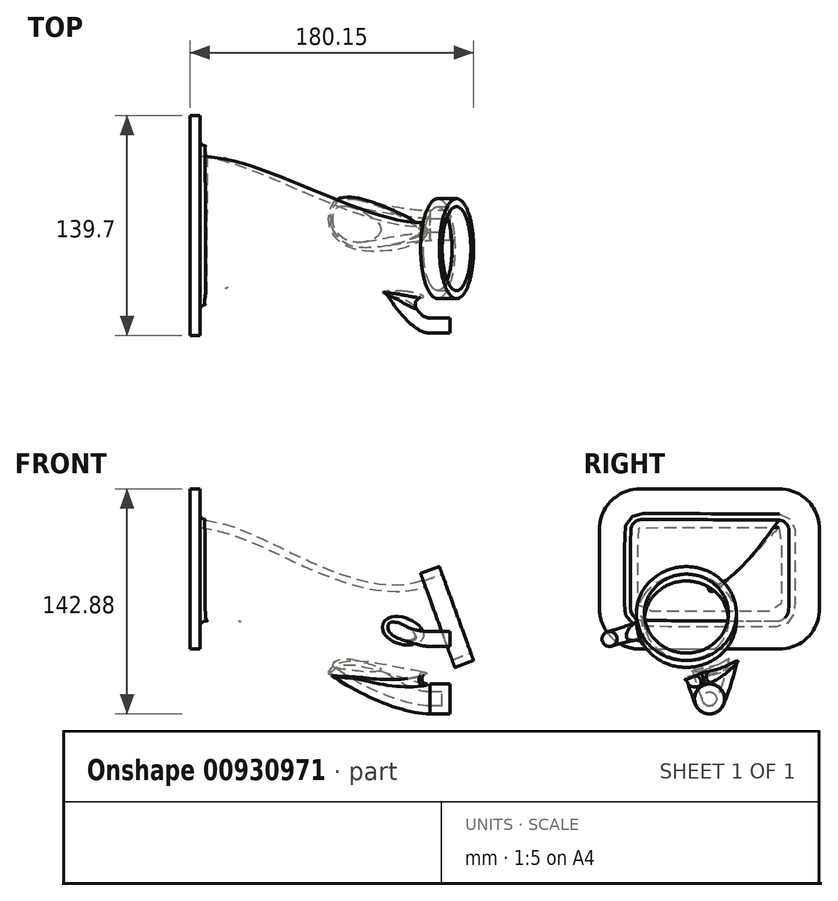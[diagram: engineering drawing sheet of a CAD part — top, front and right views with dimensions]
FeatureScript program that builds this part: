
annotation { "Feature Type Name" : "Feature", "Feature Type Description" : "" }
export const myFeature = defineFeature(function(context is Context, id is Id, definition is map)
    precondition{}
    {
        {
            var Q0;
            Q0=qCreatedBy(makeId("Right.planeOp"),FACE);
            cPlane(context, id + "F0", {"entities" : qUnion([Q0]), "cplaneType" : CPlaneType.OFFSET, "offset" : 76.2 * mm, "width" : 152.4 * mm, "height" : 152.4 * mm});
        }
        {
            var Q0;
            Q0=qCreatedBy(makeId("Right.planeOp"),FACE);
            cPlane(context, id + "F1", {"entities" : qUnion([Q0]), "cplaneType" : CPlaneType.OFFSET, "offset" : 76.2 * mm, "oppositeDirection" : true, "width" : 152.4 * mm, "height" : 152.4 * mm});
        }
        {
            var Q0;
            Q0=qCreatedBy(id+"F1.planeOp",FACE);
            var sketch = newSketch(context, id + "F2", { "sketchPlane" : qUnion([Q0])});
            skLineSegment(sketch, "E0.bottom", {"start": v(44.45, 57.15) * mm, "end": v(-44.45, 57.15) * mm});
            skLineSegment(sketch, "E0.top", {"start": v(44.45, -6.35) * mm, "end": v(-44.45, -6.35) * mm});
            skLineSegment(sketch, "E0.left", {"start": v(50.8, 50.8) * mm, "end": v(50.8, 0) * mm});
            skLineSegment(sketch, "E0.right", {"start": v(-50.8, 50.8) * mm, "end": v(-50.8, 0) * mm});
            skPoint(sketch, "E0.middle", {"position": v(0, 25.4) * mm});
            skPoint(sketch, "E1.visualSharp", {"position": v(-50.8, 57.15) * mm});
            skArc(sketch, "E1.filletArc", {"start": v(-44.45, 57.15) * mm, "mid": v(-48.94, 55.3) * mm, "end": v(-50.8, 50.8) * mm});
            skPoint(sketch, "E2.visualSharp", {"position": v(50.8, 57.15) * mm});
            skArc(sketch, "E2.filletArc", {"start": v(50.8, 50.8) * mm, "mid": v(48.94, 55.3) * mm, "end": v(44.45, 57.15) * mm});
            skPoint(sketch, "E3.visualSharp", {"position": v(50.8, -6.35) * mm});
            skArc(sketch, "E3.filletArc", {"start": v(44.45, -6.35) * mm, "mid": v(48.94, -4.5) * mm, "end": v(50.8, 0) * mm});
            skPoint(sketch, "E4.visualSharp", {"position": v(-50.8, -6.35) * mm});
            skArc(sketch, "E4.filletArc", {"start": v(-50.8, 0) * mm, "mid": v(-48.94, -4.5) * mm, "end": v(-44.45, -6.35) * mm});
            skSolve(sketch);
        }
        {
            var Q0;
            Q0=qCreatedBy(makeId("Right.planeOp"),FACE);
            var sketch = newSketch(context, id + "F3", { "sketchPlane" : qUnion([Q0])});
            skCircle(sketch, "E5", {"center": v(0, 0) * mm, "radius": 38.1 * mm});
            skSolve(sketch);
        }
        {
            var Q0;
            Q0=qCreatedBy(id+"F0.planeOp",FACE);
            var sketch = newSketch(context, id + "F4", { "sketchPlane" : qUnion([Q0])});
            skLineSegment(sketch, "E6", {"start": v(65.38, 6.35) * mm, "end": v(-65.38, 6.35) * mm, "construction": true});
            skSolve(sketch);
        }
        {
            var Q0;
            Q0=sQuery(id+"F4.wireOp",EDGE,"E6");
            cPlane(context, id + "F5", {"entities" : qUnion([Q0]), "cplaneType" : CPlaneType.LINE_ANGLE, "offset" : 25.4 * mm, "angle" : 70 * degree, "oppositeDirection" : true, "width" : 152.4 * mm, "height" : 152.4 * mm});
        }
        {
            var Q0;
            Q0=qCreatedBy(id+"F5.planeOp",FACE);
            var sketch = newSketch(context, id + "F6", { "sketchPlane" : qUnion([Q0])});
            skCircle(sketch, "E7", {"center": v(14.69, -34.6) * mm, "radius": 31.75 * mm});
            skSolve(sketch);
        }
        {
            var Q0;
            Q0=makeQuery(id+"F2.imprint","IMPRINT",FACE,{"disambiguationData":[TD([[makeQuery(id+"F2.imprint","IMPRINT",EDGE,{"derivedFrom":sQuery(id+"F2.wireOp",EDGE,"E0.bottom")}),1.0]])]});
            var Q1;
            Q1=makeQuery(id+"F3.imprint","IMPRINT",FACE,{"disambiguationData":[TD([[makeQuery(id+"F3.imprint","IMPRINT",EDGE,{"derivedFrom":sQuery(id+"F3.wireOp",EDGE,"E5")}),1.0]])]});
            var Q2;
            Q2=makeQuery(id+"F6.imprint","IMPRINT",FACE,{"disambiguationData":[TD([[makeQuery(id+"F6.imprint","IMPRINT",EDGE,{"derivedFrom":sQuery(id+"F6.wireOp",EDGE,"E7")}),1.0]])]});
            loft(context, id + "F7", {"startCondition" : LoftEndDerivativeType.NORMAL_TO_PROFILE, "startMagnitude" : 1, "endCondition" : LoftEndDerivativeType.NORMAL_TO_PROFILE, "endMagnitude" : 1, "sheetProfilesArray" : [{ "sheetProfileEntities" : qUnion([Q0]) }, { "sheetProfileEntities" : qUnion([Q1]) }, { "sheetProfileEntities" : qUnion([Q2]) }]});
        }
        {
            var Q0;
            Q0=makeQuery(id+"F7.opLoft","CAP_FACE",FACE,{"disambiguationData":[OSD([makeQuery(id+"F6.imprint","IMPRINT",FACE,{"disambiguationData":[TD([[makeQuery(id+"F6.imprint","IMPRINT",EDGE,{"derivedFrom":sQuery(id+"F6.wireOp",EDGE,"E7")}),1.0]])]})])],"isStart":true});
            extrude(context, id + "F8", {"entities" : qUnion([Q0]), "operationType" : NewBodyOperationType.ADD, "depth" : 12.7 * mm, "offsetDistance" : 25.4 * mm});
        }
        {
            var Q0;
            Q0=qCreatedBy(id+"F1.planeOp",FACE);
            cPlane(context, id + "F9", {"entities" : qUnion([Q0]), "cplaneType" : CPlaneType.OFFSET, "offset" : 152.4 * mm, "width" : 152.4 * mm, "height" : 152.4 * mm});
        }
        {
            var Q0;
            Q0=qCreatedBy(id+"F9.planeOp",FACE);
            var sketch = newSketch(context, id + "F10", { "sketchPlane" : qUnion([Q0])});
            skCircle(sketch, "E8", {"center": v(0, -57.15) * mm, "radius": 9.53 * mm});
            skSolve(sketch);
        }
        {
            var Q0;
            Q0=qCreatedBy(makeId("Right.planeOp"),FACE);
            var sketch = newSketch(context, id + "F11", { "sketchPlane" : qUnion([Q0])});
            skCircle(sketch, "E9", {"center": v(0, -12.7) * mm, "radius": 12.7 * mm});
            skSolve(sketch);
        }
        {
            var Q1;
            Q1=makeQuery(id+"F10.imprint","IMPRINT",FACE,{"disambiguationData":[TD([[makeQuery(id+"F10.imprint","IMPRINT",EDGE,{"derivedFrom":sQuery(id+"F10.wireOp",EDGE,"E8")}),1.0]])]});
            var Q2;
            Q2 = qSketchRegion(id + "F11", true);
            loft(context, id + "F12", {"operationType" : NewBodyOperationType.ADD, "startCondition" : LoftEndDerivativeType.NORMAL_TO_PROFILE, "startMagnitude" : 1, "endCondition" : LoftEndDerivativeType.TANGENT_TO_PROFILE, "endMagnitude" : 1, "sheetProfilesArray" : [{ "sheetProfileEntities" : qUnion([Q1]) }, { "sheetProfileEntities" : qUnion([Q2]) }]});
        }
        {
            var Q0;
            Q0=qCreatedBy(id+"F9.planeOp",FACE);
            var sketch = newSketch(context, id + "F13", { "sketchPlane" : qUnion([Q0])});
            skCircle(sketch, "E10", {"center": v(-63.5, -19.05) * mm, "radius": 4.76 * mm});
            skSolve(sketch);
        }
        {
            var Q0;
            Q0=qCreatedBy(makeId("Front.planeOp"),FACE);
            var sketch = newSketch(context, id + "F14", { "sketchPlane" : qUnion([Q0])});
            skCircle(sketch, "E11", {"center": v(38.1, 0) * mm, "radius": 12.7 * mm});
            skSolve(sketch);
        }
        {
            var Q1;
            Q1=makeQuery(id+"F13.imprint","IMPRINT",FACE,{"disambiguationData":[TD([[makeQuery(id+"F13.imprint","IMPRINT",EDGE,{"derivedFrom":sQuery(id+"F13.wireOp",EDGE,"E10")}),1.0]])]});
            var Q2;
            Q2 = qSketchRegion(id + "F14", true);
            loft(context, id + "F15", {"operationType" : NewBodyOperationType.ADD, "startCondition" : LoftEndDerivativeType.NORMAL_TO_PROFILE, "startMagnitude" : 1, "sheetProfilesArray" : [{ "sheetProfileEntities" : qUnion([Q1]) }, { "sheetProfileEntities" : qUnion([Q2]) }]});
        }
        {
            var Q0;
            Q0=makeQuery(id+"F15.opLoft","CAP_FACE",FACE,{"disambiguationData":[OSD([makeQuery(id+"F13.imprint","IMPRINT",FACE,{"disambiguationData":[TD([[makeQuery(id+"F13.imprint","IMPRINT",EDGE,{"derivedFrom":sQuery(id+"F13.wireOp",EDGE,"E10")}),1.0]])]})])],"isStart":true});
            extrude(context, id + "F16", {"entities" : qUnion([Q0]), "operationType" : NewBodyOperationType.ADD, "depth" : 12.7 * mm, "offsetDistance" : 25.4 * mm});
        }
        {
            var Q0;
            Q0=makeQuery(id+"F12.opLoft","CAP_FACE",FACE,{"disambiguationData":[OSD([makeQuery(id+"F10.imprint","IMPRINT",FACE,{"disambiguationData":[TD([[makeQuery(id+"F10.imprint","IMPRINT",EDGE,{"derivedFrom":sQuery(id+"F10.wireOp",EDGE,"E8")}),1.0]])]})])],"isStart":true});
            extrude(context, id + "F17", {"entities" : qUnion([Q0]), "operationType" : NewBodyOperationType.ADD, "depth" : 12.7 * mm, "offsetDistance" : 25.4 * mm});
        }
        {
            var Q0;
            Q0=makeQuery(id+"F8.opExtrude","CAP_FACE",FACE,{"disambiguationData":[OSD([makeQuery(id+"F6.imprint","IMPRINT",FACE,{"disambiguationData":[TD([[makeQuery(id+"F6.imprint","IMPRINT",EDGE,{"derivedFrom":sQuery(id+"F6.wireOp",EDGE,"E7")}),1.0]])]})])],"isStart":false});
            var Q1;
            Q1=makeQuery(id+"F7.opLoft","CAP_FACE",FACE,{"disambiguationData":[OSD([makeQuery(id+"F2.imprint","IMPRINT",FACE,{"disambiguationData":[TD([[makeQuery(id+"F2.imprint","IMPRINT",EDGE,{"derivedFrom":sQuery(id+"F2.wireOp",EDGE,"E0.bottom")}),1.0]])]})])],"isStart":true});
            shell(context, id + "F18", {"entities" : qUnion([Q0, Q1]), "thickness" : 5.08 * mm});
        }
        {
            var Q0;
            Q0=qCreatedBy(id+"F1.planeOp",FACE);
            var sketch = newSketch(context, id + "F19", { "sketchPlane" : qUnion([Q0])});
            skFitSpline(sketch, "E12.0", {"points": [v(69.85, 50.8) * mm, v(69.85, 51.31) * mm, v(69.82, 52.32) * mm, v(69.69, 53.78) * mm, v(69.52, 54.93) * mm, v(69.35, 55.8) * mm, v(69.22, 56.44) * mm, v(69.07, 57.06) * mm, v(68.85, 57.87) * mm, v(68.55, 58.86) * mm, v(68.21, 59.8) * mm, v(67.92, 60.5) * mm, v(67.7, 61.02) * mm, v(67.48, 61.53) * mm, v(67.16, 62.19) * mm, v(66.74, 63) * mm, v(66.3, 63.77) * mm, v(65.93, 64.37) * mm, v(65.65, 64.8) * mm, v(65.36, 65.22) * mm, v(64.97, 65.78) * mm, v(64.45, 66.47) * mm, v(63.9, 67.14) * mm, v(63.46, 67.65) * mm, v(63.12, 68.03) * mm, v(62.77, 68.4) * mm, v(62.29, 68.89) * mm, v(61.65, 69.5) * mm, v(60.98, 70.09) * mm, v(60.43, 70.55) * mm, v(60, 70.88) * mm, v(59.57, 71.21) * mm, v(58.96, 71.65) * mm, v(58.16, 72.2) * mm, v(57.3, 72.71) * mm, v(56.6, 73.1) * mm, v(56.06, 73.4) * mm, v(55.5, 73.67) * mm, v(54.72, 74.04) * mm, v(53.68, 74.48) * mm, v(52.58, 74.87) * mm, v(51.66, 75.16) * mm, v(50.96, 75.36) * mm, v(50.24, 75.54) * mm, v(49.23, 75.76) * mm, v(47.9, 75.98) * mm, v(46.22, 76.16) * mm, v(45.04, 76.2) * mm, v(44.45, 76.2) * mm]});
            skFitSpline(sketch, "E12.1", {"points": [v(69.85, 0) * mm, v(69.85, 16.93) * mm, v(69.85, 33.87) * mm, v(69.85, 50.8) * mm]});
            skFitSpline(sketch, "E12.2", {"points": [v(44.45, 76.2) * mm, v(14.82, 76.2) * mm, v(-14.82, 76.2) * mm, v(-44.45, 76.2) * mm]});
            skFitSpline(sketch, "E12.3", {"points": [v(44.45, -25.4) * mm, v(45.04, -25.4) * mm, v(46.22, -25.36) * mm, v(47.9, -25.18) * mm, v(49.23, -24.96) * mm, v(50.24, -24.74) * mm, v(50.96, -24.56) * mm, v(51.66, -24.36) * mm, v(52.58, -24.07) * mm, v(53.68, -23.68) * mm, v(54.72, -23.24) * mm, v(55.5, -22.87) * mm, v(56.06, -22.6) * mm, v(56.6, -22.3) * mm, v(57.3, -21.91) * mm, v(58.16, -21.4) * mm, v(58.96, -20.85) * mm, v(59.57, -20.41) * mm, v(60, -20.08) * mm, v(60.43, -19.75) * mm, v(60.98, -19.29) * mm, v(61.65, -18.7) * mm, v(62.29, -18.09) * mm, v(62.77, -17.6) * mm, v(63.12, -17.23) * mm, v(63.46, -16.85) * mm, v(63.9, -16.34) * mm, v(64.45, -15.67) * mm, v(64.97, -14.98) * mm, v(65.36, -14.42) * mm, v(65.65, -14) * mm, v(65.93, -13.57) * mm, v(66.3, -12.97) * mm, v(66.74, -12.2) * mm, v(67.16, -11.39) * mm, v(67.48, -10.73) * mm, v(67.7, -10.22) * mm, v(67.92, -9.7) * mm, v(68.21, -9) * mm, v(68.55, -8.06) * mm, v(68.85, -7.07) * mm, v(69.07, -6.26) * mm, v(69.22, -5.64) * mm, v(69.35, -5) * mm, v(69.52, -4.13) * mm, v(69.69, -2.98) * mm, v(69.82, -1.52) * mm, v(69.85, -0.51) * mm, v(69.85, 0) * mm]});
            skFitSpline(sketch, "E12.4", {"points": [v(-44.45, 76.2) * mm, v(-45.04, 76.2) * mm, v(-46.22, 76.16) * mm, v(-47.9, 75.98) * mm, v(-49.23, 75.76) * mm, v(-50.24, 75.54) * mm, v(-50.96, 75.36) * mm, v(-51.66, 75.16) * mm, v(-52.58, 74.87) * mm, v(-53.68, 74.48) * mm, v(-54.72, 74.04) * mm, v(-55.5, 73.67) * mm, v(-56.06, 73.4) * mm, v(-56.6, 73.1) * mm, v(-57.3, 72.71) * mm, v(-58.16, 72.2) * mm, v(-58.96, 71.65) * mm, v(-59.57, 71.21) * mm, v(-60, 70.88) * mm, v(-60.43, 70.55) * mm, v(-60.98, 70.09) * mm, v(-61.65, 69.5) * mm, v(-62.29, 68.89) * mm, v(-62.77, 68.4) * mm, v(-63.12, 68.03) * mm, v(-63.46, 67.65) * mm, v(-63.9, 67.14) * mm, v(-64.45, 66.47) * mm, v(-64.97, 65.78) * mm, v(-65.36, 65.22) * mm, v(-65.65, 64.8) * mm, v(-65.93, 64.37) * mm, v(-66.3, 63.77) * mm, v(-66.74, 63) * mm, v(-67.16, 62.19) * mm, v(-67.48, 61.53) * mm, v(-67.7, 61.02) * mm, v(-67.92, 60.5) * mm, v(-68.21, 59.8) * mm, v(-68.55, 58.86) * mm, v(-68.85, 57.87) * mm, v(-69.07, 57.06) * mm, v(-69.22, 56.44) * mm, v(-69.35, 55.8) * mm, v(-69.52, 54.93) * mm, v(-69.69, 53.78) * mm, v(-69.82, 52.32) * mm, v(-69.85, 51.31) * mm, v(-69.85, 50.8) * mm]});
            skFitSpline(sketch, "E12.5", {"points": [v(-69.85, 50.8) * mm, v(-69.85, 33.87) * mm, v(-69.85, 16.93) * mm, v(-69.85, 0) * mm]});
            skFitSpline(sketch, "E12.6", {"points": [v(-69.85, 0) * mm, v(-69.85, -0.51) * mm, v(-69.82, -1.52) * mm, v(-69.69, -2.98) * mm, v(-69.52, -4.13) * mm, v(-69.35, -5) * mm, v(-69.22, -5.64) * mm, v(-69.07, -6.26) * mm, v(-68.85, -7.07) * mm, v(-68.55, -8.06) * mm, v(-68.21, -9) * mm, v(-67.92, -9.7) * mm, v(-67.7, -10.22) * mm, v(-67.48, -10.73) * mm, v(-67.16, -11.39) * mm, v(-66.74, -12.2) * mm, v(-66.3, -12.97) * mm, v(-65.93, -13.57) * mm, v(-65.65, -14) * mm, v(-65.36, -14.42) * mm, v(-64.97, -14.98) * mm, v(-64.45, -15.67) * mm, v(-63.9, -16.34) * mm, v(-63.46, -16.85) * mm, v(-63.12, -17.23) * mm, v(-62.77, -17.6) * mm, v(-62.29, -18.09) * mm, v(-61.65, -18.7) * mm, v(-60.98, -19.29) * mm, v(-60.43, -19.75) * mm, v(-60, -20.08) * mm, v(-59.57, -20.41) * mm, v(-58.96, -20.85) * mm, v(-58.16, -21.4) * mm, v(-57.3, -21.91) * mm, v(-56.6, -22.3) * mm, v(-56.06, -22.6) * mm, v(-55.5, -22.87) * mm, v(-54.72, -23.24) * mm, v(-53.68, -23.68) * mm, v(-52.58, -24.07) * mm, v(-51.66, -24.36) * mm, v(-50.96, -24.56) * mm, v(-50.24, -24.74) * mm, v(-49.23, -24.96) * mm, v(-47.9, -25.18) * mm, v(-46.22, -25.36) * mm, v(-45.04, -25.4) * mm, v(-44.45, -25.4) * mm]});
            skFitSpline(sketch, "E12.7", {"points": [v(-44.45, -25.4) * mm, v(-14.82, -25.4) * mm, v(14.82, -25.4) * mm, v(44.45, -25.4) * mm]});
            skFitSpline(sketch, "E13.0", {"points": [v(-45.46, -3.67) * mm, v(-45.36, -3.7) * mm, v(-45.26, -3.72) * mm, v(-45.16, -3.74) * mm, v(-45.06, -3.76) * mm, v(-44.95, -3.78) * mm, v(-44.85, -3.8) * mm, v(-44.74, -3.8) * mm, v(-44.65, -3.8) * mm, v(-44.52, -3.81) * mm, v(-44.43, -3.81) * mm, v(-44.36, -3.81) * mm, v(-44.33, -3.8) * mm, v(-44.31, -3.8) * mm, v(-44.28, -3.8) * mm, v(-44.22, -3.81) * mm, v(-44.15, -3.81) * mm, v(-44.06, -3.81) * mm, v(-43.94, -3.8) * mm, v(-43.81, -3.8) * mm, v(-43.63, -3.81) * mm, v(-43.4, -3.81) * mm, v(-43.14, -3.8) * mm, v(-42.87, -3.8) * mm, v(-42.51, -3.81) * mm, v(-42.06, -3.8) * mm, v(-41.52, -3.81) * mm, v(-40.99, -3.81) * mm, v(-40.27, -3.8) * mm, v(-39.37, -3.81) * mm, v(-38.3, -3.8) * mm, v(-37.22, -3.81) * mm, v(-36.14, -3.8) * mm, v(-35.07, -3.8) * mm, v(-33.63, -3.81) * mm, v(-31.84, -3.8) * mm, v(-29.69, -3.81) * mm, v(-27.54, -3.8) * mm, v(-25.38, -3.81) * mm, v(-22.51, -3.8) * mm, v(-18.93, -3.81) * mm, v(-14.62, -3.8) * mm, v(-10.32, -3.81) * mm, v(-6.01, -3.8) * mm, v(-1.7, -3.81) * mm, v(2.6, -3.8) * mm, v(6.9, -3.81) * mm, v(11.2, -3.8) * mm, v(15.5, -3.81) * mm, v(19.1, -3.8) * mm, v(21.97, -3.81) * mm, v(24.12, -3.81) * mm, v(26.27, -3.8) * mm, v(28.42, -3.81) * mm, v(30.57, -3.8) * mm, v(32.37, -3.81) * mm, v(33.8, -3.8) * mm, v(34.88, -3.8) * mm, v(35.96, -3.81) * mm, v(37.03, -3.81) * mm, v(38.1, -3.8) * mm, v(39.18, -3.81) * mm, v(40.08, -3.8) * mm, v(40.8, -3.81) * mm, v(41.34, -3.81) * mm, v(41.87, -3.8) * mm, v(42.41, -3.81) * mm, v(42.86, -3.8) * mm, v(43.17, -3.81) * mm, v(43.35, -3.81) * mm, v(43.49, -3.81) * mm, v(43.62, -3.8) * mm, v(43.76, -3.8) * mm, v(43.89, -3.81) * mm, v(44.03, -3.81) * mm, v(44.15, -3.8) * mm, v(44.21, -3.8) * mm, v(44.25, -3.8) * mm, v(44.27, -3.8) * mm, v(44.3, -3.81) * mm, v(44.35, -3.81) * mm, v(44.44, -3.81) * mm, v(44.57, -3.8) * mm, v(44.69, -3.8) * mm, v(44.79, -3.8) * mm, v(44.9, -3.79) * mm, v(45.03, -3.77) * mm, v(45.2, -3.74) * mm, v(45.4, -3.7) * mm, v(45.65, -3.62) * mm, v(45.97, -3.5) * mm, v(46.33, -3.32) * mm, v(46.67, -3.1) * mm, v(46.99, -2.85) * mm, v(47.27, -2.57) * mm, v(47.53, -2.26) * mm, v(47.75, -1.92) * mm, v(47.94, -1.55) * mm, v(48.06, -1.24) * mm, v(48.13, -0.99) * mm, v(48.18, -0.8) * mm, v(48.2, -0.64) * mm, v(48.23, -0.5) * mm, v(48.24, -0.38) * mm, v(48.25, -0.27) * mm, v(48.26, -0.14) * mm, v(48.26, -0.02) * mm, v(48.26, 0.07) * mm, v(48.26, 0.12) * mm, v(48.26, 0.15) * mm, v(48.26, 0.18) * mm, v(48.26, 0.22) * mm, v(48.26, 0.27) * mm, v(48.26, 0.34) * mm, v(48.26, 0.43) * mm, v(48.26, 0.55) * mm, v(48.26, 0.68) * mm, v(48.26, 0.86) * mm, v(48.26, 1.09) * mm, v(48.26, 1.36) * mm, v(48.26, 1.63) * mm, v(48.26, 1.99) * mm, v(48.26, 2.44) * mm, v(48.26, 2.98) * mm, v(48.26, 3.52) * mm, v(48.26, 4.06) * mm, v(48.26, 4.79) * mm, v(48.26, 5.69) * mm, v(48.26, 6.77) * mm, v(48.26, 7.85) * mm, v(48.26, 8.94) * mm, v(48.26, 10.38) * mm, v(48.26, 12.19) * mm, v(48.26, 14.35) * mm, v(48.26, 16.52) * mm, v(48.26, 18.68) * mm, v(48.26, 20.85) * mm, v(48.26, 23.02) * mm, v(48.26, 25.9) * mm, v(48.26, 28.8) * mm, v(48.26, 31.68) * mm, v(48.26, 33.84) * mm, v(48.26, 36) * mm, v(48.26, 38.18) * mm, v(48.26, 39.98) * mm, v(48.26, 41.42) * mm, v(48.26, 42.5) * mm, v(48.26, 43.59) * mm, v(48.26, 44.67) * mm, v(48.26, 45.76) * mm, v(48.26, 46.66) * mm, v(48.26, 47.38) * mm, v(48.26, 47.92) * mm, v(48.26, 48.37) * mm, v(48.26, 48.73) * mm, v(48.26, 49) * mm, v(48.26, 49.27) * mm, v(48.26, 49.55) * mm, v(48.26, 49.82) * mm, v(48.26, 50.04) * mm, v(48.26, 50.22) * mm, v(48.26, 50.36) * mm, v(48.26, 50.47) * mm, v(48.26, 50.56) * mm, v(48.26, 50.62) * mm, v(48.26, 50.68) * mm, v(48.26, 50.73) * mm, v(48.26, 50.77) * mm, v(48.26, 50.82) * mm, v(48.26, 50.89) * mm, v(48.26, 50.97) * mm, v(48.25, 51.07) * mm, v(48.24, 51.18) * mm, v(48.23, 51.33) * mm, v(48.2, 51.5) * mm, v(48.15, 51.71) * mm, v(48.08, 51.98) * mm, v(47.98, 52.24) * mm, v(47.86, 52.5) * mm, v(47.76, 52.7) * mm, v(47.64, 52.88) * mm, v(47.48, 53.12) * mm, v(47.25, 53.4) * mm, v(46.94, 53.7) * mm, v(46.6, 53.96) * mm, v(46.23, 54.18) * mm, v(45.9, 54.33) * mm, v(45.62, 54.43) * mm, v(45.42, 54.49) * mm, v(45.22, 54.53) * mm, v(45.04, 54.57) * mm, v(44.88, 54.59) * mm, v(44.78, 54.6) * mm, v(44.67, 54.6) * mm, v(44.54, 54.6) * mm, v(44.43, 54.61) * mm, v(44.36, 54.61) * mm, v(44.33, 54.6) * mm, v(44.3, 54.6) * mm, v(44.26, 54.6) * mm, v(44.2, 54.6) * mm, v(44.14, 54.6) * mm, v(44.04, 54.61) * mm, v(43.92, 54.61) * mm, v(43.77, 54.6) * mm, v(43.63, 54.6) * mm, v(43.44, 54.6) * mm, v(43.2, 54.61) * mm, v(42.92, 54.61) * mm, v(42.63, 54.6) * mm, v(42.35, 54.6) * mm, v(41.97, 54.61) * mm, v(41.5, 54.6) * mm, v(40.92, 54.6) * mm, v(40.35, 54.61) * mm, v(39.78, 54.61) * mm, v(39.02, 54.6) * mm, v(38.07, 54.61) * mm, v(36.92, 54.6) * mm, v(35.78, 54.6) * mm, v(34.64, 54.61) * mm, v(33.5, 54.61) * mm, v(31.97, 54.6) * mm, v(30.07, 54.61) * mm, v(27.79, 54.6) * mm, v(25.5, 54.61) * mm, v(23.22, 54.6) * mm, v(20.93, 54.6) * mm, v(17.89, 54.61) * mm, v(14.08, 54.6) * mm, v(9.51, 54.61) * mm, v(4.94, 54.6) * mm, v(0.37, 54.6) * mm, v(-4.2, 54.61) * mm, v(-8.76, 54.6) * mm, v(-13.33, 54.61) * mm, v(-17.14, 54.6) * mm, v(-20.18, 54.61) * mm, v(-22.47, 54.61) * mm, v(-24.75, 54.6) * mm, v(-27.04, 54.61) * mm, v(-29.32, 54.6) * mm, v(-31.6, 54.61) * mm, v(-33.5, 54.6) * mm, v(-35.03, 54.61) * mm, v(-36.17, 54.61) * mm, v(-37.32, 54.6) * mm, v(-38.46, 54.61) * mm, v(-39.4, 54.6) * mm, v(-40.17, 54.61) * mm, v(-40.74, 54.61) * mm, v(-41.31, 54.6) * mm, v(-41.88, 54.6) * mm, v(-42.36, 54.61) * mm, v(-42.74, 54.6) * mm, v(-43.03, 54.6) * mm, v(-43.31, 54.61) * mm, v(-43.55, 54.61) * mm, v(-43.74, 54.6) * mm, v(-43.88, 54.6) * mm, v(-44, 54.61) * mm, v(-44.1, 54.61) * mm, v(-44.17, 54.61) * mm, v(-44.23, 54.6) * mm, v(-44.27, 54.6) * mm, v(-44.3, 54.6) * mm, v(-44.33, 54.61) * mm, v(-44.39, 54.61) * mm, v(-44.49, 54.61) * mm, v(-44.63, 54.6) * mm, v(-44.76, 54.6) * mm, v(-44.88, 54.59) * mm, v(-45, 54.57) * mm, v(-45.15, 54.55) * mm, v(-45.33, 54.5) * mm, v(-45.54, 54.45) * mm, v(-45.81, 54.36) * mm, v(-46.1, 54.24) * mm, v(-46.36, 54.1) * mm, v(-46.62, 53.94) * mm, v(-46.93, 53.7) * mm, v(-47.25, 53.4) * mm, v(-47.54, 53.04) * mm, v(-47.79, 52.65) * mm, v(-47.98, 52.25) * mm, v(-48.1, 51.9) * mm, v(-48.18, 51.6) * mm, v(-48.22, 51.37) * mm, v(-48.24, 51.18) * mm, v(-48.25, 51.04) * mm, v(-48.26, 50.93) * mm, v(-48.26, 50.83) * mm, v(-48.26, 50.76) * mm, v(-48.26, 50.7) * mm, v(-48.26, 50.67) * mm, v(-48.26, 50.64) * mm, v(-48.26, 50.6) * mm, v(-48.26, 50.54) * mm, v(-48.26, 50.47) * mm, v(-48.26, 50.36) * mm, v(-48.26, 50.23) * mm, v(-48.26, 50.08) * mm, v(-48.26, 49.93) * mm, v(-48.26, 49.78) * mm, v(-48.26, 49.62) * mm, v(-48.26, 49.42) * mm, v(-48.26, 49.17) * mm, v(-48.26, 48.86) * mm, v(-48.26, 48.56) * mm, v(-48.26, 48.15) * mm, v(-48.26, 47.64) * mm, v(-48.26, 47.03) * mm, v(-48.26, 46.43) * mm, v(-48.26, 45.82) * mm, v(-48.26, 45.2) * mm, v(-48.26, 44.4) * mm, v(-48.26, 43.38) * mm, v(-48.26, 42.16) * mm, v(-48.26, 40.94) * mm, v(-48.26, 39.73) * mm, v(-48.26, 38.5) * mm, v(-48.26, 36.89) * mm, v(-48.26, 34.86) * mm, v(-48.26, 32.42) * mm, v(-48.26, 29.98) * mm, v(-48.26, 27.55) * mm, v(-48.26, 25.11) * mm, v(-48.26, 22.68) * mm, v(-48.26, 20.24) * mm, v(-48.26, 17.8) * mm, v(-48.26, 15.37) * mm, v(-48.26, 13.34) * mm, v(-48.26, 11.71) * mm, v(-48.26, 10.5) * mm, v(-48.26, 9.28) * mm, v(-48.26, 8.06) * mm, v(-48.26, 6.84) * mm, v(-48.26, 5.83) * mm, v(-48.26, 5.02) * mm, v(-48.26, 4.4) * mm, v(-48.26, 3.8) * mm, v(-48.26, 3.19) * mm, v(-48.26, 2.68) * mm, v(-48.26, 2.28) * mm, v(-48.26, 1.97) * mm, v(-48.26, 1.67) * mm, v(-48.26, 1.36) * mm, v(-48.26, 1.1) * mm, v(-48.26, 0.9) * mm, v(-48.26, 0.75) * mm, v(-48.26, 0.6) * mm, v(-48.26, 0.44) * mm, v(-48.26, 0.32) * mm, v(-48.26, 0.23) * mm, v(-48.26, 0.2) * mm, v(-48.26, 0.16) * mm, v(-48.26, 0.12) * mm, v(-48.26, 0.06) * mm, v(-48.26, -0.05) * mm, v(-48.26, -0.2) * mm, v(-48.24, -0.34) * mm, v(-48.23, -0.46) * mm, v(-48.22, -0.58) * mm, v(-48.19, -0.74) * mm, v(-48.15, -0.94) * mm, v(-48.08, -1.16) * mm, v(-47.98, -1.44) * mm, v(-47.82, -1.79) * mm, v(-47.58, -2.18) * mm, v(-47.3, -2.54) * mm, v(-46.97, -2.87) * mm, v(-46.6, -3.15) * mm, v(-46.28, -3.35) * mm, v(-46.01, -3.48) * mm, v(-45.83, -3.55) * mm, v(-45.68, -3.6) * mm, v(-45.57, -3.64) * mm, v(-45.46, -3.67) * mm, v(-45.36, -3.7) * mm, v(-45.26, -3.72) * mm, v(-45.46, -3.67) * mm]});
            skSolve(sketch);
        }
        {
            var Q0;
            Q0=makeQuery(id+"F19.imprint","IMPRINT",FACE,{"disambiguationData":[TD([[makeQuery(id+"F19.imprint","IMPRINT",EDGE,{"derivedFrom":sQuery(id+"F19.wireOp",EDGE,"E12.0")}),1.0]])]});
            extrude(context, id + "F20", {"entities" : qUnion([Q0]), "operationType" : NewBodyOperationType.ADD, "depth" : 6.35 * mm, "offsetDistance" : 25.4 * mm});
        }
        {
            var Q0;
            Q0=makeQuery(id+"F20.boolean.opBoolean","INTERSECT",EDGE,{"derivedFrom":[makeQuery(id+"F7.opLoft","SWEPT_FACE",FACE,{"disambiguationData":[OSD([sQuery(id+"F2.wireOp",EDGE,"E0.bottom"),sQuery(id+"F2.wireOp",EDGE,"E0.top"),sQuery(id+"F2.wireOp",EDGE,"E0.left"),sQuery(id+"F2.wireOp",EDGE,"E0.right"),sQuery(id+"F2.wireOp",EDGE,"E1.filletArc"),sQuery(id+"F2.wireOp",EDGE,"E2.filletArc"),sQuery(id+"F2.wireOp",EDGE,"E3.filletArc"),sQuery(id+"F2.wireOp",EDGE,"E4.filletArc"),sQuery(id+"F3.wireOp",EDGE,"E5"),sQuery(id+"F6.wireOp",EDGE,"E7")])]}),makeQuery(id+"F20.opExtrude","CAP_FACE",FACE,{"disambiguationData":[OSD([sQuery(id+"F19.wireOp",EDGE,"E12.0"),sQuery(id+"F19.wireOp",EDGE,"E12.1"),sQuery(id+"F19.wireOp",EDGE,"E12.2"),sQuery(id+"F19.wireOp",EDGE,"E12.3"),sQuery(id+"F19.wireOp",EDGE,"E12.4"),sQuery(id+"F19.wireOp",EDGE,"E12.5"),sQuery(id+"F19.wireOp",EDGE,"E12.6"),sQuery(id+"F19.wireOp",EDGE,"E12.7"),sQuery(id+"F19.wireOp",EDGE,"E13.0")])],"isStart":false})]});
            fillet(context, id + "F21", {"entities" : qUnion([Q0]), "radius" : 3.8 * mm, "tangentPropagation" : true, "allowEdgeOverflow" : false});
        }
        {
            var Q0;
            Q0=makeQuery(id+"F12.boolean.opBoolean","INTERSECT",EDGE,{"derivedFrom":[makeQuery(id+"F7.opLoft","SWEPT_FACE",FACE,{"disambiguationData":[OSD([sQuery(id+"F2.wireOp",EDGE,"E0.bottom"),sQuery(id+"F2.wireOp",EDGE,"E0.top"),sQuery(id+"F2.wireOp",EDGE,"E0.left"),sQuery(id+"F2.wireOp",EDGE,"E0.right"),sQuery(id+"F2.wireOp",EDGE,"E1.filletArc"),sQuery(id+"F2.wireOp",EDGE,"E2.filletArc"),sQuery(id+"F2.wireOp",EDGE,"E3.filletArc"),sQuery(id+"F2.wireOp",EDGE,"E4.filletArc"),sQuery(id+"F3.wireOp",EDGE,"E5"),sQuery(id+"F6.wireOp",EDGE,"E7")])]}),makeQuery(id+"F12.opLoft","SWEPT_FACE",FACE,{"disambiguationData":[OSD([sQuery(id+"F10.wireOp",EDGE,"E8"),sQuery(id+"F11.wireOp",EDGE,"E9")])]})]});
            fillet(context, id + "F22", {"entities" : qUnion([Q0]), "radius" : 3.8 * mm, "tangentPropagation" : true, "allowEdgeOverflow" : false});
        }
        {
            var Q0;
            Q0=makeQuery(id+"F15.boolean.opBoolean","INTERSECT",EDGE,{"derivedFrom":[makeQuery(id+"F7.opLoft","SWEPT_FACE",FACE,{"disambiguationData":[OSD([sQuery(id+"F2.wireOp",EDGE,"E0.bottom"),sQuery(id+"F2.wireOp",EDGE,"E0.top"),sQuery(id+"F2.wireOp",EDGE,"E0.left"),sQuery(id+"F2.wireOp",EDGE,"E0.right"),sQuery(id+"F2.wireOp",EDGE,"E1.filletArc"),sQuery(id+"F2.wireOp",EDGE,"E2.filletArc"),sQuery(id+"F2.wireOp",EDGE,"E3.filletArc"),sQuery(id+"F2.wireOp",EDGE,"E4.filletArc"),sQuery(id+"F3.wireOp",EDGE,"E5"),sQuery(id+"F6.wireOp",EDGE,"E7")])]}),makeQuery(id+"F15.opLoft","SWEPT_FACE",FACE,{"disambiguationData":[OSD([sQuery(id+"F13.wireOp",EDGE,"E10"),sQuery(id+"F14.wireOp",EDGE,"E11")])]})]});
            fillet(context, id + "F23", {"entities" : qUnion([Q0]), "radius" : 5.08 * mm, "tangentPropagation" : true, "allowEdgeOverflow" : false});
        }
    });
